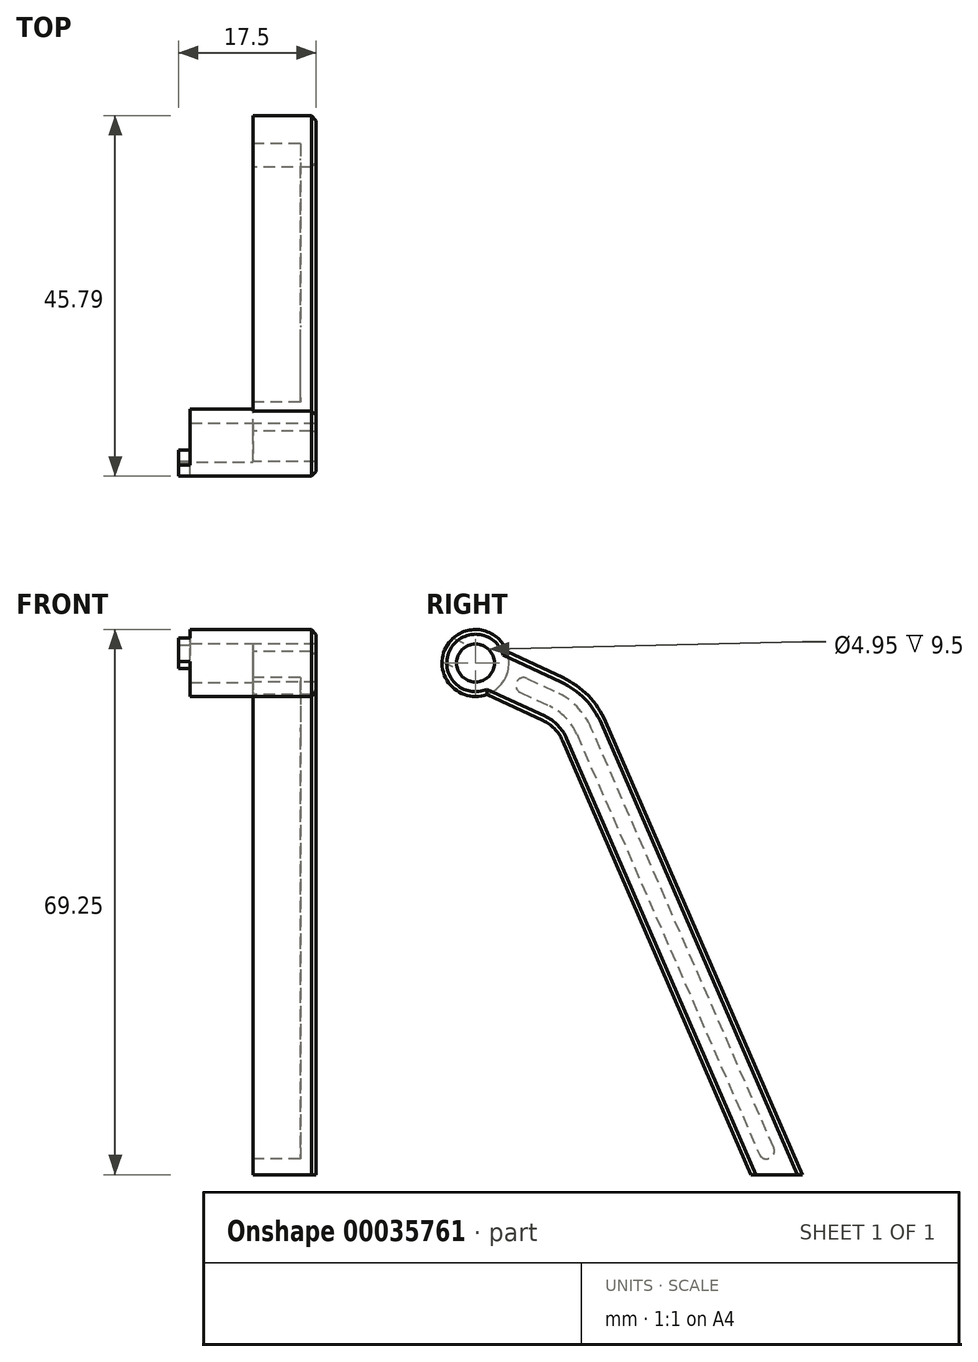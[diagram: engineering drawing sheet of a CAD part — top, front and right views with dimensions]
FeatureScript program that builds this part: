
annotation { "Feature Type Name" : "Feature", "Feature Type Description" : "" }
export const myFeature = defineFeature(function(context is Context, id is Id, definition is map)
    precondition{}
    {
        {
            var Q0;
            Q0=qCreatedBy(makeId("Right.planeOp"),FACE);
            var sketch = newSketch(context, id + "F0", { "sketchPlane" : qUnion([Q0])});
            skCircle(sketch, "E0", {"center": v(0, 0) * mm, "radius": 2.4 * mm});
            skArc(sketch, "E1", {"start": v(4, 1.45) * mm, "mid": v(-3.85, 1.8) * mm, "end": v(1.46, -4) * mm});
            skLineSegment(sketch, "E2", {"start": v(0, 0) * mm, "end": v(20.38, -9.5) * mm, "construction": true});
            skLineSegment(sketch, "E3", {"start": v(0, 0) * mm, "end": v(23.49, 0) * mm, "construction": true});
            skLineSegment(sketch, "E4", {"start": v(4, 1.45) * mm, "end": v(11.1, -1.86) * mm});
            skLineSegment(sketch, "E5", {"start": v(1.46, -4) * mm, "end": v(8.56, -7.3) * mm});
            skLineSegment(sketch, "E6", {"start": v(0, -65) * mm, "end": v(66.6, -65) * mm, "construction": true});
            skLineSegment(sketch, "E7", {"start": v(0, -65) * mm, "end": v(0, 0) * mm, "construction": true});
            skLineSegment(sketch, "E8", {"start": v(11.03, -9.84) * mm, "end": v(35, -65) * mm});
            skLineSegment(sketch, "E9", {"start": v(35, -65) * mm, "end": v(41.54, -65) * mm});
            skLineSegment(sketch, "E10", {"start": v(41.54, -65) * mm, "end": v(16.53, -7.45) * mm});
            skPoint(sketch, "E11.visualSharp", {"position": v(10.28, -8.1) * mm});
            skArc(sketch, "E11.filletArc", {"start": v(11.03, -9.84) * mm, "mid": v(10.03, -8.34) * mm, "end": v(8.56, -7.3) * mm});
            skPoint(sketch, "E12.visualSharp", {"position": v(14.87, -3.62) * mm});
            skArc(sketch, "E12.filletArc", {"start": v(16.53, -7.45) * mm, "mid": v(14.32, -4.16) * mm, "end": v(11.1, -1.86) * mm});
            skSolve(sketch);
        }
        {
            var Q0;
            Q0=makeQuery(id+"F0.imprint","IMPRINT",FACE,{"disambiguationData":[TD([[makeQuery(id+"F0.imprint","IMPRINT",EDGE,{"derivedFrom":sQuery(id+"F0.wireOp",EDGE,"E0")}),-1.0]])]});
            extrude(context, id + "F1", {"entities" : qUnion([Q0]), "depth" : 8 * mm});
        }
        {
            var Q0;
            Q0=makeQuery(id+"F1.opExtrude","CAP_FACE",FACE,{"disambiguationData":[OSD([sQuery(id+"F0.wireOp",EDGE,"E0"),sQuery(id+"F0.wireOp",EDGE,"E1"),sQuery(id+"F0.wireOp",EDGE,"E4"),sQuery(id+"F0.wireOp",EDGE,"E5"),sQuery(id+"F0.wireOp",EDGE,"E8"),sQuery(id+"F0.wireOp",EDGE,"E9"),sQuery(id+"F0.wireOp",EDGE,"E10"),sQuery(id+"F0.wireOp",EDGE,"E11.filletArc"),sQuery(id+"F0.wireOp",EDGE,"E12.filletArc")])],"isStart":true});
            var sketch = newSketch(context, id + "F2", { "sketchPlane" : qUnion([Q0])});
            skCircle(sketch, "E13", {"center": v(0, 0) * mm, "radius": 4.25 * mm});
            skCircle(sketch, "E14", {"center": v(0, 0) * mm, "radius": 2.47 * mm});
            skSolve(sketch);
        }
        {
            var Q0;
            Q0 = qSketchRegion(id + "F2", true);
            extrude(context, id + "F3", {"entities" : qUnion([Q0]), "operationType" : NewBodyOperationType.ADD, "depth" : 8 * mm});
        }
        {
            var Q0;
            Q0=makeQuery(id+"F3.opExtrude","CAP_FACE",FACE,{"disambiguationData":[OSD([sQuery(id+"F2.wireOp",EDGE,"E13"),sQuery(id+"F2.wireOp",EDGE,"E14")])],"isStart":false});
            var sketch = newSketch(context, id + "F4", { "sketchPlane" : qUnion([Q0])});
            skLineSegment(sketch, "E15", {"start": v(0, 0) * mm, "end": v(7.07, 3.3) * mm, "construction": true});
            skLineSegment(sketch, "E16", {"start": v(4.25, 0.16) * mm, "end": v(2.37, -0.72) * mm});
            skLineSegment(sketch, "E17", {"start": v(2.85, 3.15) * mm, "end": v(0.97, 2.27) * mm});
            skArc(sketch, "E18.0", {"start": v(2.37, -0.72) * mm, "mid": v(2.24, 1.05) * mm, "end": v(0.97, 2.27) * mm});
            skArc(sketch, "E19.0", {"start": v(4.25, 0.16) * mm, "mid": v(3.85, 1.8) * mm, "end": v(2.85, 3.15) * mm});
            skSolve(sketch);
        }
        {
            var Q0;
            Q0=makeQuery(id+"F4.imprint","IMPRINT",FACE,{"disambiguationData":[TD([[makeQuery(id+"F4.imprint","IMPRINT",EDGE,{"derivedFrom":sQuery(id+"F4.wireOp",EDGE,"E16")}),-1.0]])]});
            extrude(context, id + "F5", {"entities" : qUnion([Q0]), "operationType" : NewBodyOperationType.ADD, "depth" : 1.5 * mm});
        }
        {
            var Q0;
            {var subQ0=sQuery(id+"F0.wireOp",EDGE,"E1");var subQ1=sQuery(id+"F0.wireOp",EDGE,"E4");var subQ2=sQuery(id+"F0.wireOp",EDGE,"E5");var subQ3=sQuery(id+"F0.wireOp",EDGE,"E8");var subQ4=sQuery(id+"F0.wireOp",EDGE,"E9");var subQ5=sQuery(id+"F0.wireOp",EDGE,"E10");var subQ6=sQuery(id+"F0.wireOp",EDGE,"E11.filletArc");var subQ7=sQuery(id+"F0.wireOp",EDGE,"E12.filletArc");Q0=makeQuery(id+"F3.boolean.opBoolean","SPLIT",FACE,{"disambiguationData":[TD([makeQuery(id+"F1.opExtrude","SWEPT_FACE",FACE,{"disambiguationData":[OSD([subQ0])]})])],"derivedFrom":makeQuery(id+"F1.opExtrude","CAP_FACE",FACE,{"disambiguationData":[OSD([sQuery(id+"F0.wireOp",EDGE,"E0"),subQ0,subQ1,subQ2,subQ3,subQ4,subQ5,subQ6,subQ7])],"isStart":true})});}
            var sketch = newSketch(context, id + "F6", { "sketchPlane" : qUnion([Q0])});
            skLineSegment(sketch, "E20.0", {"start": v(-6.54, -1.95) * mm, "end": v(-10.25, -3.68) * mm});
            skArc(sketch, "E20.1", {"start": v(-14.7, -8.25) * mm, "mid": v(-12.9, -5.55) * mm, "end": v(-10.25, -3.68) * mm});
            skLineSegment(sketch, "E20.2", {"start": v(-37.88, -61.6) * mm, "end": v(-14.7, -8.25) * mm});
            skLineSegment(sketch, "E21.0", {"start": v(-12.86, -9.04) * mm, "end": v(-36.05, -62.4) * mm});
            skArc(sketch, "E21.1", {"start": v(-12.86, -9.04) * mm, "mid": v(-11.46, -6.95) * mm, "end": v(-9.4, -5.49) * mm});
            skLineSegment(sketch, "E21.2", {"start": v(-5.7, -3.76) * mm, "end": v(-9.4, -5.49) * mm});
            skArc(sketch, "E22", {"start": v(-36.05, -62.4) * mm, "mid": v(-37.37, -62.92) * mm, "end": v(-37.88, -61.6) * mm});
            skArc(sketch, "E23", {"start": v(-5.7, -3.76) * mm, "mid": v(-5.21, -2.43) * mm, "end": v(-6.54, -1.95) * mm});
            skSolve(sketch);
        }
        {
            var Q0;
            Q0 = qSketchRegion(id + "F6", true);
            extrude(context, id + "F7", {"entities" : qUnion([Q0]), "operationType" : NewBodyOperationType.REMOVE, "oppositeDirection" : true, "depth" : 6 * mm});
        }
        {
            var Q0;
            Q0=makeQuery(id+"F1.opExtrude","CAP_EDGE",EDGE,{"disambiguationData":[OSD([sQuery(id+"F0.wireOp",EDGE,"E12.filletArc")])],"isStart":false});
            var Q1;
            Q1=makeQuery(id+"F1.opExtrude","CAP_EDGE",EDGE,{"disambiguationData":[OSD([sQuery(id+"F0.wireOp",EDGE,"E4")])],"isStart":false});
            var Q2;
            Q2=makeQuery(id+"F1.opExtrude","CAP_EDGE",EDGE,{"disambiguationData":[OSD([sQuery(id+"F0.wireOp",EDGE,"E1")])],"isStart":false});
            var Q3;
            Q3=makeQuery(id+"F1.opExtrude","CAP_EDGE",EDGE,{"disambiguationData":[OSD([sQuery(id+"F0.wireOp",EDGE,"E5")])],"isStart":false});
            var Q4;
            Q4=makeQuery(id+"F1.opExtrude","CAP_EDGE",EDGE,{"disambiguationData":[OSD([sQuery(id+"F0.wireOp",EDGE,"E11.filletArc")])],"isStart":false});
            chamfer(context, id + "F8", {"entities" : qUnion([Q0, Q1, Q2, Q3, Q4]), "width" : 0.6 * mm, "tangentPropagation" : true});
        }
    });
